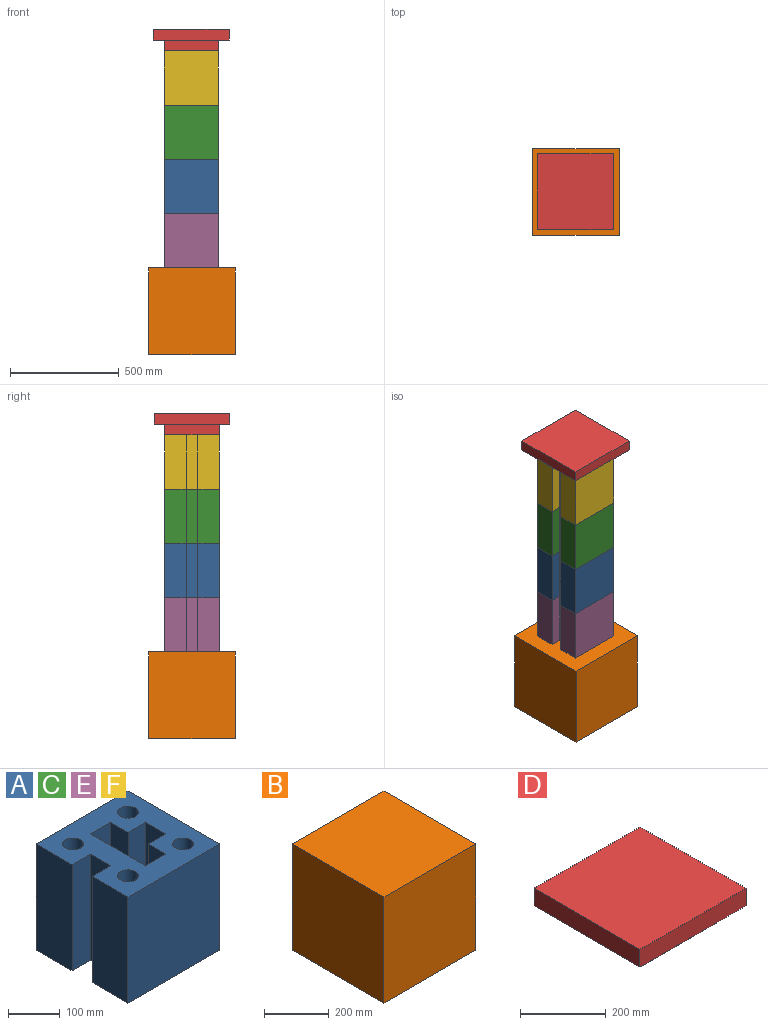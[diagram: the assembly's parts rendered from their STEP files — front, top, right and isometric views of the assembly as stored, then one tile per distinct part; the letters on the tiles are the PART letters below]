
ASSEMBLY  parts=6 mates=5
PART A: 22 faces, bbox 250x250x250 mm
  f0: plane 250x50mm, normal (0,1,0), area 12500mm2, adj f1,f19,f20,f21
  f1: plane 250x97.5mm, normal (-1,0,0), area 24375mm2, adj f0,f2,f20,f21
  f2: plane 250x250mm, normal (0,-1,0), area 62500mm2, adj f1,f3,f20,f21
  f3: plane 250x250mm, normal (1,0,0), area 62500mm2, adj f2,f4,f20,f21
  f4: plane 250x250mm, normal (0,1,0), area 62500mm2, adj f3,f5,f20,f21
  f5: plane 250x97.5mm, normal (-1,0,0), area 24375mm2, adj f4,f6,f20,f21
  f6: plane 250x50mm, normal (0,-1,0), area 12500mm2, adj f5,f19,f20,f21
  f7: plane 250x55mm, normal (0,-1,0), area 13750mm2, adj f8,f14,f20,f21
  f8: plane 250x47.5mm, normal (-1,0,0), area 11875mm2, adj f7,f9,f20,f21
  f9: plane 250x47.5mm, normal (0,-1,0), area 11875mm2, adj f8,f10,f20,f21
  f10: plane 250x55mm, normal (-1,0,0), area 13750mm2, adj f9,f11,f20,f21
  f11: plane 250x47.5mm, normal (0,1,0), area 11875mm2, adj f10,f12,f20,f21
  f12: plane 250x47.5mm, normal (-1,0,0), area 11875mm2, adj f11,f13,f20,f21
  f13: plane 250x55mm, normal (0,1,0), area 13750mm2, adj f12,f14,f20,f21
  f14: plane 250x150mm, normal (1,0,0), area 37500mm2, adj f7,f13,f20,f21
  f15: cylinder r=20mm len=250mm, axis (0,0,-1), area 31415.9mm2, adj f20,f21
  f16: cylinder r=20mm len=250mm, axis (0,0,-1), area 31415.9mm2, adj f20,f21
  f17: cylinder r=20mm len=250mm, axis (0,0,-1), area 31415.9mm2, adj f20,f21
  f18: cylinder r=20mm len=250mm, axis (0,0,-1), area 31415.9mm2, adj f20,f21
  f19: plane 250x55mm, normal (-1,0,0), area 13750mm2, adj f0,f6,f20,f21
  f20: plane 250x250mm, normal (0,0,1), area 43861mm2, adj f0,f1,f2,f3,f4,f5,f6,f7
  f21: plane 250x250mm, normal (0,0,-1), area 43861mm2, adj f0,f1,f2,f3,f4,f5,f6,f7
PART B: 6 faces, bbox 400x400x400 mm
  f0: plane 400x400mm, normal (0,-1,0), area 160000mm2, adj f1,f3,f4,f5
  f1: plane 400x400mm, normal (1,0,0), area 160000mm2, adj f0,f2,f4,f5
  f2: plane 400x400mm, normal (0,1,0), area 160000mm2, adj f1,f3,f4,f5
  f3: plane 400x400mm, normal (-1,0,0), area 160000mm2, adj f0,f2,f4,f5
  f4: plane 400x400mm, normal (0,0,1), area 160000mm2, adj f0,f1,f2,f3
  f5: plane 400x400mm, normal (0,0,-1), area 160000mm2, adj f0,f1,f2,f3
PART C: same geometry as A
PART D: 11 faces, bbox 350x350x100 mm
  f0: plane 350x50mm, normal (0,-1,0), area 17500mm2, adj f1,f3,f4,f5
  f1: plane 350x50mm, normal (1,0,0), area 17500mm2, adj f0,f2,f4,f5
  f2: plane 350x50mm, normal (0,1,0), area 17500mm2, adj f1,f3,f4,f5
  f3: plane 350x50mm, normal (-1,0,0), area 17500mm2, adj f0,f2,f4,f5
  f4: plane 350x350mm, normal (0,0,1), area 122500mm2, adj f0,f1,f2,f3
  f5: plane 350x350mm, normal (0,0,-1), area 60000mm2, adj f0,f1,f2,f3,f6,f7,f8,f9
  f6: plane 250x50mm, normal (1,0,0), area 12500mm2, adj f5,f7,f9,f10
  f7: plane 250x50mm, normal (0,1,0), area 12500mm2, adj f5,f6,f8,f10
  f8: plane 250x50mm, normal (-1,0,0), area 12500mm2, adj f5,f7,f9,f10
  f9: plane 250x50mm, normal (0,-1,0), area 12500mm2, adj f5,f6,f8,f10
  f10: plane 250x250mm, normal (0,0,-1), area 62500mm2, adj f6,f7,f8,f9
PART E: same geometry as A
PART F: same geometry as A
PLACE A t=(-4.45,-2.49,572.33)mm
PLACE B t=(-1.23,-2.49,-2.67)mm fixed
PLACE C t=(-4.45,-2.49,822.33)mm
PLACE D t=(-4.45,-2.49,1247.33)mm
PLACE E t=(-4.45,-2.49,322.33)mm
PLACE F t=(-4.45,-2.49,1072.33)mm
MATE fastened E.f21 <-> B.f4  axis (0,0,-1) through (-1.23,-2.49,197.33)mm
MATE fastened A.f21 <-> E.f20  axis (0,0,-1) through (-1.23,-2.49,447.33)mm
MATE fastened D.f10 <-> F.f20  axis (0,0,-1) through (120.55,-127.49,1197.33)mm
MATE fastened C.f21 <-> A.f20  axis (0,0,-1) through (120.55,-127.49,697.33)mm
MATE fastened F.f21 <-> C.f20  axis (0,0,-1) through (120.55,-127.49,947.33)mm
